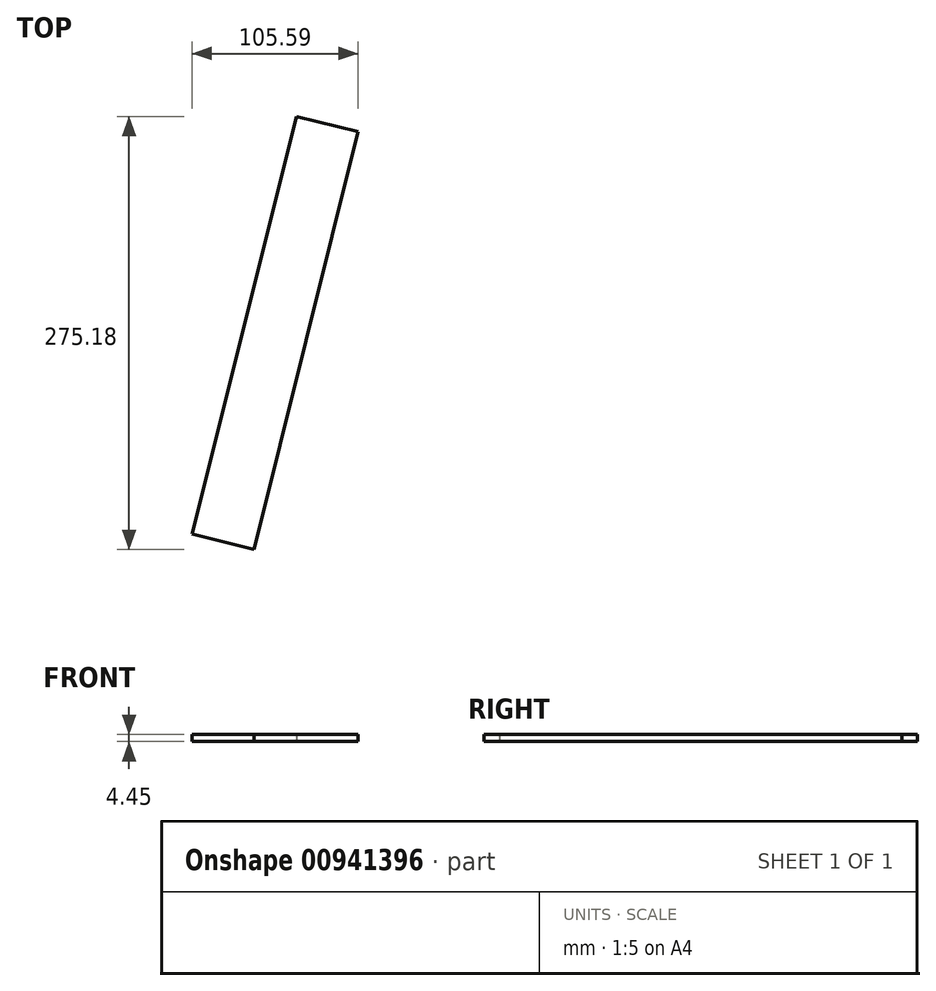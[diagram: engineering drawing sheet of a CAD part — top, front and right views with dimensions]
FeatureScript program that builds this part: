
annotation { "Feature Type Name" : "Feature", "Feature Type Description" : "" }
export const myFeature = defineFeature(function(context is Context, id is Id, definition is map)
    precondition{}
    {
        {
            var Q0;
            Q0=qCreatedBy(makeId("Top.planeOp"),FACE);
            var sketch = newSketch(context, id + "F0", { "sketchPlane" : qUnion([Q0])});
            skPoint(sketch, "E0.middle", {"position": v(26.92, -27.29) * mm});
            skPoint(sketch, "E1.middle", {"position": v(6.29, -16.09) * mm});
            skLineSegment(sketch, "E2", {"start": v(26.02, 106.02) * mm, "end": v(-40.28, -159.34) * mm});
            skLineSegment(sketch, "E3", {"start": v(26.02, 106.02) * mm, "end": v(-13.27, 115.84) * mm});
            skLineSegment(sketch, "E4", {"start": v(-13.27, 115.84) * mm, "end": v(-79.57, -149.52) * mm});
            skLineSegment(sketch, "E5", {"start": v(-79.57, -149.52) * mm, "end": v(-40.28, -159.34) * mm});
            skSolve(sketch);
        }
        {
            var Q0;
            Q0=makeQuery(id+"F0.imprint","IMPRINT",FACE,{"disambiguationData":[TD([[makeQuery(id+"F0.imprint","IMPRINT",EDGE,{"derivedFrom":sQuery(id+"F0.wireOp",EDGE,"E2")}),-1.0]])]});
            extrude(context, id + "F1", {"entities" : qUnion([Q0]), "depth" : 4.45 * mm, "offsetDistance" : 25 * mm});
        }
    });
